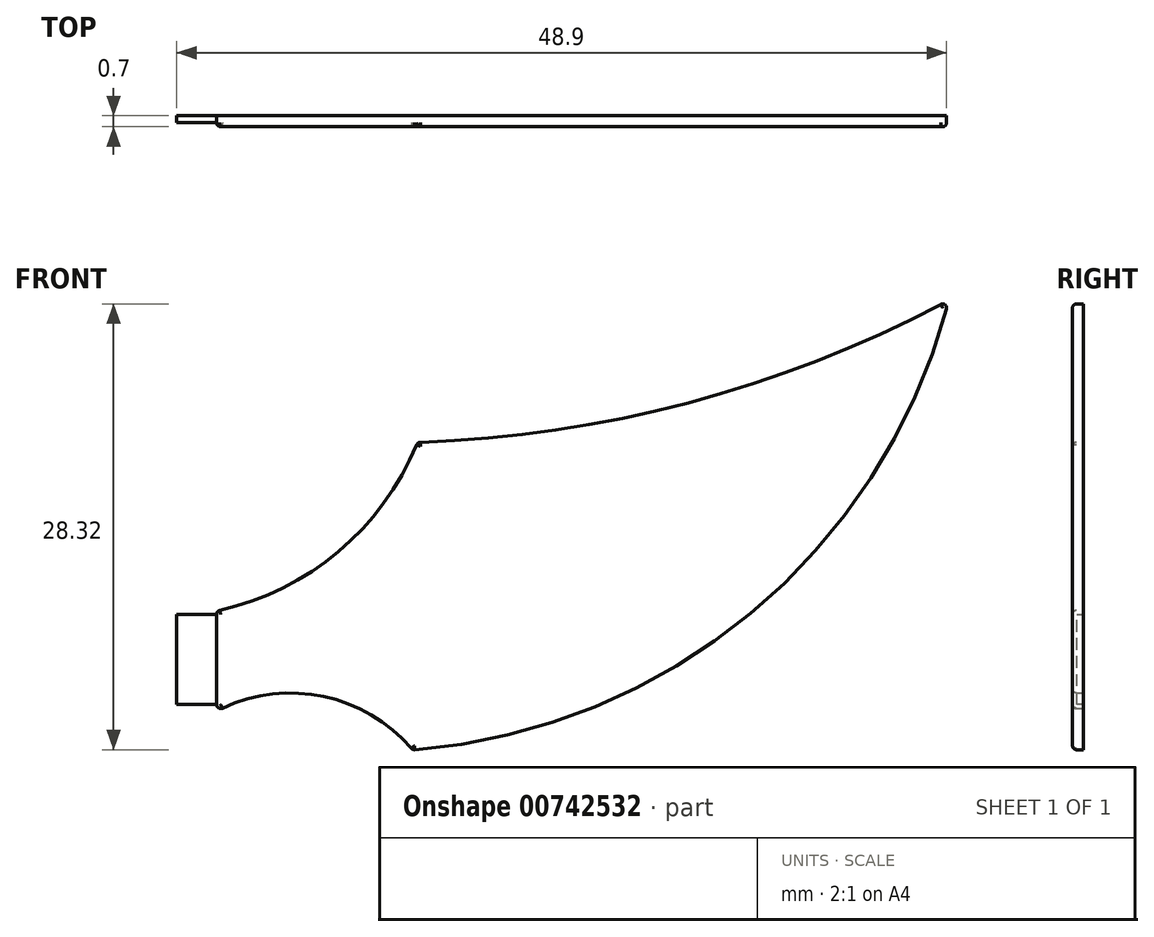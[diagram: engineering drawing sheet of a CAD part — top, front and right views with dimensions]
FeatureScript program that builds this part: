
annotation { "Feature Type Name" : "Feature", "Feature Type Description" : "" }
export const myFeature = defineFeature(function(context is Context, id is Id, definition is map)
    precondition{}
    {
        {
            var Q0;
            Q0=qCreatedBy(makeId("Front.planeOp"),FACE);
            var sketch = newSketch(context, id + "F0", { "sketchPlane" : qUnion([Q0])});
            skLineSegment(sketch, "E0", {"start": v(0, 0) * mm, "end": v(0, 6.35) * mm});
            skLineSegment(sketch, "E1", {"start": v(0, 6.35) * mm, "end": v(12.77, 17.06) * mm, "construction": true});
            skLineSegment(sketch, "E2", {"start": v(12.77, 17.06) * mm, "end": v(46.5, 26.1) * mm, "construction": true});
            skLineSegment(sketch, "E3", {"start": v(12.77, 17.06) * mm, "end": v(12.77, 6.6) * mm, "construction": true});
            skLineSegment(sketch, "E4", {"start": v(46.5, 26.1) * mm, "end": v(12.45, -2.47) * mm, "construction": true});
            skLineSegment(sketch, "E5", {"start": v(46.5, 26.1) * mm, "end": v(46.5, 12.28) * mm, "construction": true});
            skLineSegment(sketch, "E6", {"start": v(0, 0) * mm, "end": v(12.45, -2.47) * mm, "construction": true});
            skArc(sketch, "E7", {"start": v(0, 6.35) * mm, "mid": v(7.72, 10.12) * mm, "end": v(12.77, 17.06) * mm});
            skArc(sketch, "E8", {"start": v(12.77, 17.06) * mm, "mid": v(30.16, 19.63) * mm, "end": v(46.5, 26.1) * mm});
            skArc(sketch, "E9", {"start": v(12.45, -2.47) * mm, "mid": v(34.08, 6.34) * mm, "end": v(46.5, 26.1) * mm});
            skArc(sketch, "E10", {"start": v(12.45, -2.47) * mm, "mid": v(6.66, 0.95) * mm, "end": v(0, 0) * mm});
            skSolve(sketch);
        }
        {
            var Q0;
            Q0=makeQuery(id+"F0.imprint","IMPRINT",FACE,{"disambiguationData":[TD([[makeQuery(id+"F0.imprint","IMPRINT",EDGE,{"derivedFrom":sQuery(id+"F0.wireOp",EDGE,"E0")}),-1.0]])]});
            extrude(context, id + "F1", {"entities" : qUnion([Q0]), "depth" : 1.59 * mm, "offsetDistance" : 25.4 * mm});
        }
        {
            var Q0;
            Q0=makeQuery(id+"F1.opExtrude","CAP_EDGE",EDGE,{"disambiguationData":[OSD([sQuery(id+"F0.wireOp",EDGE,"E7")])],"isStart":true});
            var Q1;
            Q1=makeQuery(id+"F1.opExtrude","CAP_EDGE",EDGE,{"disambiguationData":[OSD([sQuery(id+"F0.wireOp",EDGE,"E7")])],"isStart":false});
            var Q2;
            Q2=makeQuery(id+"F1.opExtrude","CAP_FACE",FACE,{"disambiguationData":[OSD([sQuery(id+"F0.wireOp",EDGE,"E0"),sQuery(id+"F0.wireOp",EDGE,"E7"),sQuery(id+"F0.wireOp",EDGE,"E8"),sQuery(id+"F0.wireOp",EDGE,"E9"),sQuery(id+"F0.wireOp",EDGE,"E10")])],"isStart":true});
            var Q3;
            Q3=makeQuery(id+"F1.opExtrude","CAP_FACE",FACE,{"disambiguationData":[OSD([sQuery(id+"F0.wireOp",EDGE,"E0"),sQuery(id+"F0.wireOp",EDGE,"E7"),sQuery(id+"F0.wireOp",EDGE,"E8"),sQuery(id+"F0.wireOp",EDGE,"E9"),sQuery(id+"F0.wireOp",EDGE,"E10")])],"isStart":false});
            fillet(context, id + "F2", {"entities" : qUnion([Q0, Q1, Q2, Q3]), "radius" : 0.25 * mm, "tangentPropagation" : true, "allowEdgeOverflow" : false});
        }
        {
            var Q0;
            Q0=makeQuery(id+"F1.opExtrude","SWEPT_EDGE",EDGE,{"disambiguationData":[OSD([sQuery(id+"F0.wireOp",EDGE,"E0"),sQuery(id+"F0.wireOp",EDGE,"E7")])]});
            var Q1;
            Q1=makeQuery(id+"F1.opExtrude","SWEPT_EDGE",EDGE,{"disambiguationData":[OSD([sQuery(id+"F0.wireOp",EDGE,"E0"),sQuery(id+"F0.wireOp",EDGE,"E10")])]});
            var Q2;
            Q2=makeQuery(id+"F1.opExtrude","SWEPT_EDGE",EDGE,{"disambiguationData":[OSD([sQuery(id+"F0.wireOp",EDGE,"E9"),sQuery(id+"F0.wireOp",EDGE,"E10")])]});
            var Q3;
            Q3=makeQuery(id+"F1.opExtrude","SWEPT_EDGE",EDGE,{"disambiguationData":[OSD([sQuery(id+"F0.wireOp",EDGE,"E7"),sQuery(id+"F0.wireOp",EDGE,"E8")])]});
            var Q4;
            Q4=makeQuery(id+"F1.opExtrude","SWEPT_EDGE",EDGE,{"disambiguationData":[OSD([sQuery(id+"F0.wireOp",EDGE,"E8"),sQuery(id+"F0.wireOp",EDGE,"E9")])]});
            fillet(context, id + "F3", {"entities" : qUnion([Q0, Q1, Q2, Q3, Q4]), "radius" : 0.25 * mm, "tangentPropagation" : true, "allowEdgeOverflow" : false});
        }
        {
            var Q0;
            Q0=makeQuery(id+"F1.opExtrude","SWEPT_FACE",FACE,{"disambiguationData":[OSD([sQuery(id+"F0.wireOp",EDGE,"E0")])]});
            var sketch = newSketch(context, id + "F4", { "sketchPlane" : qUnion([Q0])});
            skLineSegment(sketch, "E11.bottom", {"start": v(0.25, 6.15) * mm, "end": v(1.33, 6.15) * mm});
            skLineSegment(sketch, "E11.top", {"start": v(0.25, 0.4) * mm, "end": v(1.33, 0.4) * mm});
            skLineSegment(sketch, "E11.left", {"start": v(0.25, 6.15) * mm, "end": v(0.25, 0.4) * mm});
            skLineSegment(sketch, "E11.right", {"start": v(1.33, 6.15) * mm, "end": v(1.33, 0.4) * mm});
            skLineSegment(sketch, "E12.0", {"start": v(0.28, 6.12) * mm, "end": v(0.28, 0.43) * mm});
            skLineSegment(sketch, "E12.1", {"start": v(1.3, 6.12) * mm, "end": v(0.28, 6.12) * mm});
            skLineSegment(sketch, "E12.2", {"start": v(1.3, 0.43) * mm, "end": v(1.3, 6.12) * mm});
            skLineSegment(sketch, "E12.3", {"start": v(0.28, 0.43) * mm, "end": v(1.3, 0.43) * mm});
            skSolve(sketch);
        }
        {
            var Q0;
            Q0=makeQuery(id+"F4.imprint","IMPRINT",FACE,{"disambiguationData":[TD([[makeQuery(id+"F4.imprint","IMPRINT",EDGE,{"derivedFrom":sQuery(id+"F4.wireOp",EDGE,"E12.0")}),1.0]])]});
            extrude(context, id + "F5", {"entities" : qUnion([Q0]), "operationType" : NewBodyOperationType.ADD, "depth" : 2.54 * mm, "offsetDistance" : 25.4 * mm});
        }
        {
            var Q0;
            Q0=qCreatedBy(makeId("Front.planeOp"),FACE);
            cPlane(context, id + "F6", {"entities" : qUnion([Q0]), "cplaneType" : CPlaneType.OFFSET, "offset" : 0.89 * mm, "width" : 152.4 * mm, "height" : 152.4 * mm});
        }
        {
            var Q0;
            Q0=qCreatedBy(id+"F6.planeOp",FACE);
            var sketch = newSketch(context, id + "F7", { "sketchPlane" : qUnion([Q0])});
            skLineSegment(sketch, "E13.bottom", {"start": v(-15.73, 34.36) * mm, "end": v(67.64, 34.36) * mm});
            skLineSegment(sketch, "E13.top", {"start": v(-15.73, -18.48) * mm, "end": v(67.64, -18.48) * mm});
            skLineSegment(sketch, "E13.left", {"start": v(-15.73, 34.36) * mm, "end": v(-15.73, -18.48) * mm});
            skLineSegment(sketch, "E13.right", {"start": v(67.64, 34.36) * mm, "end": v(67.64, -18.48) * mm});
            skSolve(sketch);
        }
        {
            var Q0;
            Q0=qSketchRegion(id+"F7",true);
            extrude(context, id + "F8", {"entities" : qUnion([Q0]), "operationType" : NewBodyOperationType.REMOVE, "oppositeDirection" : true, "depth" : 25.4 * mm, "offsetDistance" : 25.4 * mm});
        }
    });
